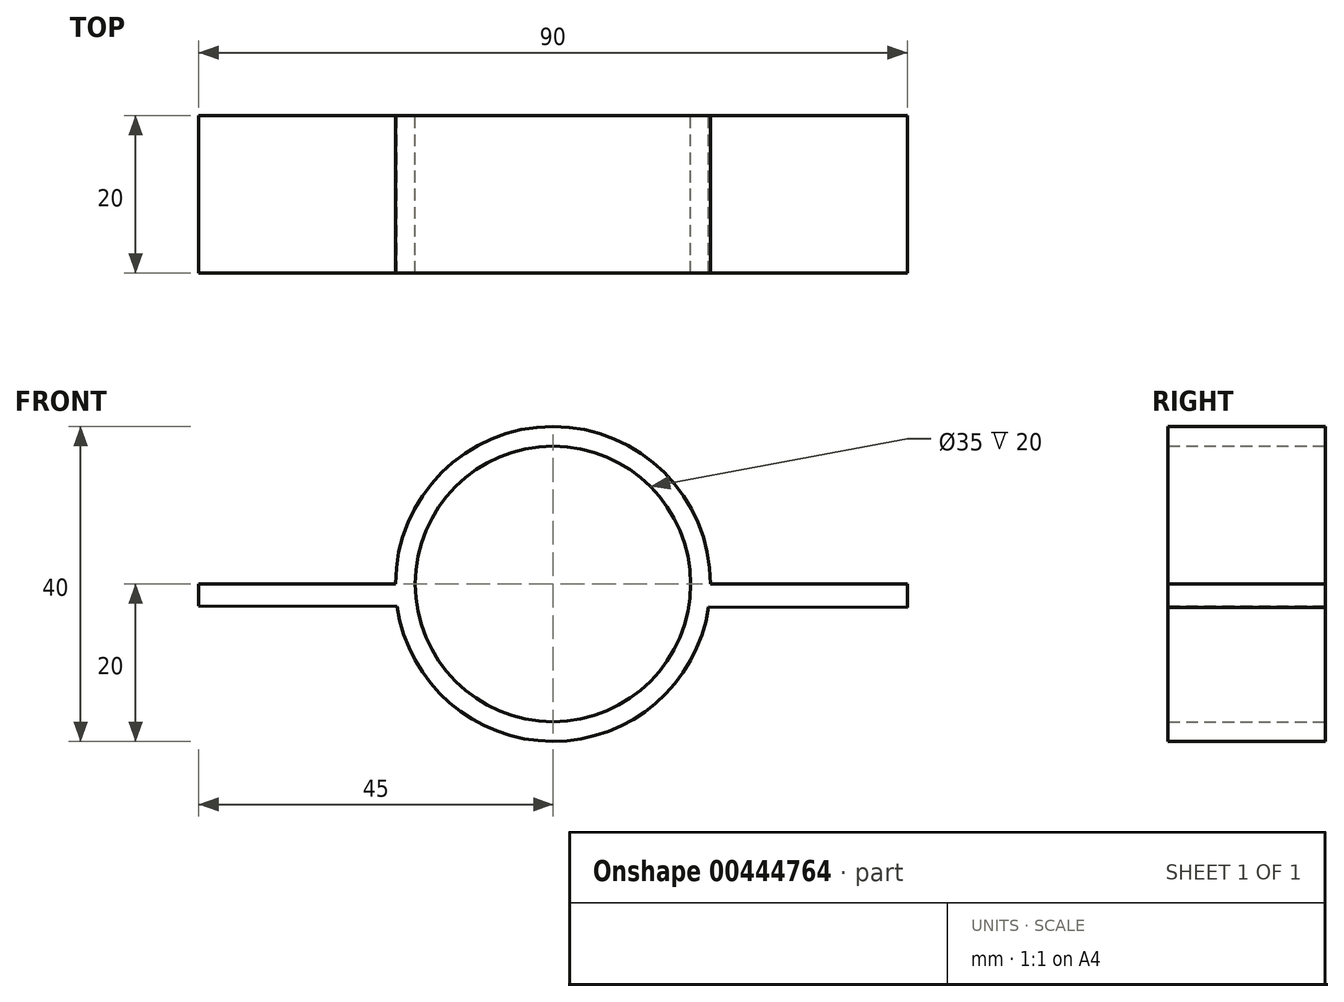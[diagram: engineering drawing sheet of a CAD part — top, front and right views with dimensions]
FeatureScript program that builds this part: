
annotation { "Feature Type Name" : "Feature", "Feature Type Description" : "" }
export const myFeature = defineFeature(function(context is Context, id is Id, definition is map)
    precondition{}
    {
        {
            var Q0;
            Q0=qCreatedBy(makeId("Front.planeOp"),FACE);
            var sketch = newSketch(context, id + "F0", { "sketchPlane" : qUnion([Q0])});
            skCircle(sketch, "E0", {"center": v(0, 0) * mm, "radius": 17.5 * mm});
            skArc(sketch, "E1", {"start": v(20, 0) * mm, "mid": v(0, 20) * mm, "end": v(-20, 0) * mm});
            skLineSegment(sketch, "E2.bottom", {"start": v(-45, 0) * mm, "end": v(-20, 0) * mm});
            skLineSegment(sketch, "E3.left", {"start": v(-45, 0) * mm, "end": v(-45, -2.78) * mm});
            skLineSegment(sketch, "E3.right", {"start": v(45, 0) * mm, "end": v(45, -3) * mm});
            skLineSegment(sketch, "E4.bottom", {"start": v(-45, -2.78) * mm, "end": v(-19.8, -2.84) * mm});
            skLineSegment(sketch, "E5.trimOffspring", {"start": v(20, 0) * mm, "end": v(45, 0) * mm});
            skLineSegment(sketch, "E6.trimOffspring", {"start": v(19.78, -2.94) * mm, "end": v(45, -3) * mm});
            skArc(sketch, "E7.trimOffspring", {"start": v(-19.8, -2.84) * mm, "mid": v(-0.05, -20) * mm, "end": v(19.78, -2.94) * mm});
            skSolve(sketch);
        }
        {
            var Q0;
            Q0=qSketchRegion(id+"F0",true);
            extrude(context, id + "F1", {"entities" : qUnion([Q0]), "depth" : 20 * mm});
        }
    });
